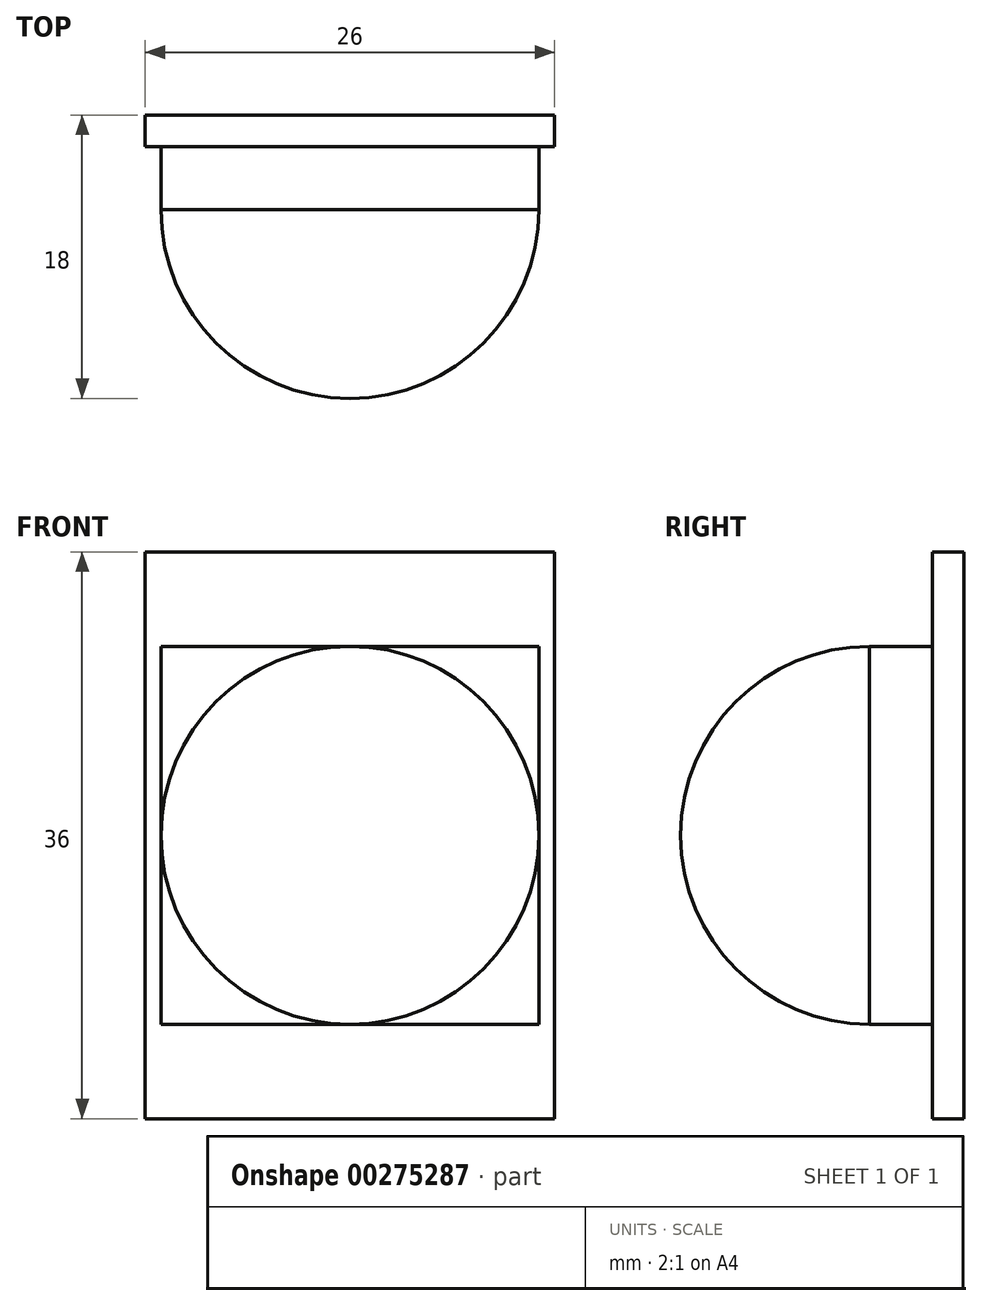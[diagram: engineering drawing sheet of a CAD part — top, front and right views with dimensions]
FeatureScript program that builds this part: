
annotation { "Feature Type Name" : "Feature", "Feature Type Description" : "" }
export const myFeature = defineFeature(function(context is Context, id is Id, definition is map)
    precondition{}
    {
        {
            var Q0;
            Q0=qCreatedBy(makeId("Front.planeOp"),FACE);
            var sketch = newSketch(context, id + "F0", { "sketchPlane" : qUnion([Q0])});
            skCircle(sketch, "E0", {"center": v(0, 0) * mm, "radius": 12 * mm});
            skLineSegment(sketch, "E1.bottom", {"start": v(12, -12) * mm, "end": v(-12, -12) * mm});
            skLineSegment(sketch, "E1.top", {"start": v(12, 12) * mm, "end": v(-12, 12) * mm});
            skLineSegment(sketch, "E1.left", {"start": v(12, -12) * mm, "end": v(12, 12) * mm});
            skLineSegment(sketch, "E1.right", {"start": v(-12, -12) * mm, "end": v(-12, 12) * mm});
            skLineSegment(sketch, "E2.bottom", {"start": v(13, -18) * mm, "end": v(-13, -18) * mm});
            skLineSegment(sketch, "E2.top", {"start": v(13, 18) * mm, "end": v(-13, 18) * mm});
            skLineSegment(sketch, "E2.left", {"start": v(13, -18) * mm, "end": v(13, 18) * mm});
            skLineSegment(sketch, "E2.right", {"start": v(-13, -18) * mm, "end": v(-13, 18) * mm});
            skPoint(sketch, "E3", {"position": v(0, 12) * mm});
            skPoint(sketch, "E4", {"position": v(0, -12) * mm});
            skLineSegment(sketch, "E5", {"start": v(0, 12) * mm, "end": v(0, -12) * mm});
            skSolve(sketch);
        }
        {
            var Q0;
            Q0 = qSketchRegion(id + "F0", true);
            var Q1;
            {var subQ0=sQuery(id+"F0.wireOp",EDGE,"E1.top");var subQ3=sQuery(id+"F0.wireOp",EDGE,"E1.right");var subQ5=makeQuery(id+"F0.imprint","INTERSECT",VERTEX,{"derivedFrom":[subQ0,subQ3]});Q1=makeQuery(id+"F0.imprint","IMPRINT",FACE,{"disambiguationData":[TD([[makeQuery(id+"F0.imprint","IMPRINT",EDGE,{"disambiguationData":[TD([[subQ5,1.0]])],"derivedFrom":subQ3}),-1.0]])]});}
            var Q2;
            {var subQ0=sQuery(id+"F0.wireOp",EDGE,"E5");Q2=makeQuery(id+"F0.imprint","IMPRINT",FACE,{"disambiguationData":[TD([[makeQuery(id+"F0.imprint","IMPRINT",EDGE,{"derivedFrom":subQ0}),-1.0]])]});}
            var Q3;
            {var subQ0=sQuery(id+"F0.wireOp",EDGE,"E5");Q3=makeQuery(id+"F0.imprint","IMPRINT",FACE,{"disambiguationData":[TD([[makeQuery(id+"F0.imprint","IMPRINT",EDGE,{"derivedFrom":subQ0}),1.0]])]});}
            var Q4;
            {var subQ0=sQuery(id+"F0.wireOp",EDGE,"E1.top");var subQ3=sQuery(id+"F0.wireOp",EDGE,"E1.left");var subQ5=makeQuery(id+"F0.imprint","INTERSECT",VERTEX,{"derivedFrom":[subQ0,subQ3]});Q4=makeQuery(id+"F0.imprint","IMPRINT",FACE,{"disambiguationData":[TD([[makeQuery(id+"F0.imprint","IMPRINT",EDGE,{"disambiguationData":[TD([[subQ5,1.0]])],"derivedFrom":subQ3}),1.0]])]});}
            var Q5;
            {var subQ0=sQuery(id+"F0.wireOp",EDGE,"E1.bottom");var subQ3=sQuery(id+"F0.wireOp",EDGE,"E1.left");var subQ5=makeQuery(id+"F0.imprint","INTERSECT",VERTEX,{"derivedFrom":[subQ0,subQ3]});Q5=makeQuery(id+"F0.imprint","IMPRINT",FACE,{"disambiguationData":[TD([[makeQuery(id+"F0.imprint","IMPRINT",EDGE,{"disambiguationData":[TD([[subQ5,-1.0]])],"derivedFrom":subQ3}),1.0]])]});}
            var Q6;
            {var subQ0=sQuery(id+"F0.wireOp",EDGE,"E1.bottom");var subQ3=sQuery(id+"F0.wireOp",EDGE,"E1.right");var subQ5=makeQuery(id+"F0.imprint","INTERSECT",VERTEX,{"derivedFrom":[subQ0,subQ3]});Q6=makeQuery(id+"F0.imprint","IMPRINT",FACE,{"disambiguationData":[TD([[makeQuery(id+"F0.imprint","IMPRINT",EDGE,{"disambiguationData":[TD([[subQ5,-1.0]])],"derivedFrom":subQ3}),-1.0]])]});}
            extrude(context, id + "F1", {"entities" : qUnion([Q0, Q1, Q2, Q3, Q4, Q5, Q6]), "depth" : 2 * mm});
        }
        {
            var Q0;
            Q0=makeQuery(id+"F1.opExtrude","CAP_FACE",FACE,{"disambiguationData":[OSD([sQuery(id+"F0.wireOp",EDGE,"E2.bottom"),sQuery(id+"F0.wireOp",EDGE,"E2.top"),sQuery(id+"F0.wireOp",EDGE,"E2.left"),sQuery(id+"F0.wireOp",EDGE,"E2.right")])],"isStart":false});
            var sketch = newSketch(context, id + "F2", { "sketchPlane" : qUnion([Q0])});
            skLineSegment(sketch, "E6.bottom", {"start": v(-12, -12) * mm, "end": v(12, -12) * mm});
            skLineSegment(sketch, "E6.top", {"start": v(-12, 12) * mm, "end": v(12, 12) * mm});
            skLineSegment(sketch, "E6.left", {"start": v(-12, -12) * mm, "end": v(-12, 12) * mm});
            skLineSegment(sketch, "E6.right", {"start": v(12, -12) * mm, "end": v(12, 12) * mm});
            skPoint(sketch, "E6.middle", {"position": v(0, 0) * mm});
            skSolve(sketch);
        }
        {
            var Q0;
            Q0 = qSketchRegion(id + "F2", true);
            extrude(context, id + "F3", {"entities" : qUnion([Q0]), "operationType" : NewBodyOperationType.ADD, "depth" : 4 * mm});
        }
        {
            var Q0;
            Q0=makeQuery(id+"F3.opExtrude","CAP_FACE",FACE,{"disambiguationData":[OSD([sQuery(id+"F2.wireOp",EDGE,"E6.bottom"),sQuery(id+"F2.wireOp",EDGE,"E6.top"),sQuery(id+"F2.wireOp",EDGE,"E6.left"),sQuery(id+"F2.wireOp",EDGE,"E6.right")])],"isStart":false});
            var sketch = newSketch(context, id + "F4", { "sketchPlane" : qUnion([Q0])});
            skCircle(sketch, "E7", {"center": v(0, 0) * mm, "radius": 12 * mm});
            skLineSegment(sketch, "E8", {"start": v(0, 12) * mm, "end": v(0, -12) * mm});
            skSolve(sketch);
        }
        {
            var Q0;
            {var subQ0=sQuery(id+"F4.wireOp",EDGE,"E8");Q0=makeQuery(id+"F4.imprint","IMPRINT",FACE,{"disambiguationData":[TD([[makeQuery(id+"F4.imprint","IMPRINT",EDGE,{"derivedFrom":subQ0}),1.0]])]});}
            var Q1;
            Q1=sQuery(id+"F4.wireOp",EDGE,"E8");
            revolve(context, id + "F5", {"operationType" : NewBodyOperationType.ADD, "entities" : qUnion([Q0]), "axis" : qUnion([Q1]), "revolveType" : RevolveType.ONE_DIRECTION, "angle" : 180 * degree});
        }
    });
